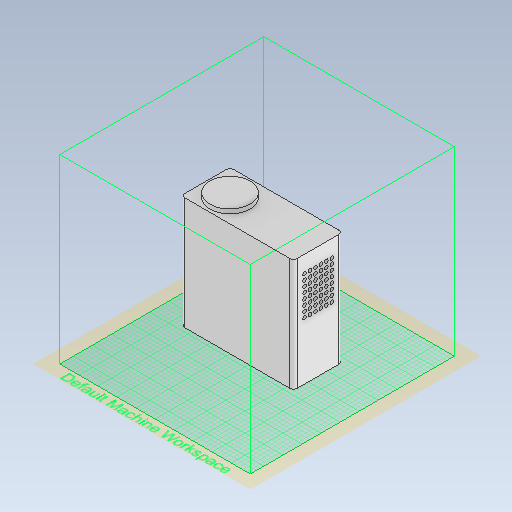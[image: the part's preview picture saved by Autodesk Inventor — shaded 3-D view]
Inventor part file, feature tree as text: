
AUTODESK INVENTOR PART (.ipt)
format: ipt  version: 2021.1 (Build 251245010, 245A)  size: 1,046,016 bytes
history: native  units: in
note: dims shown in document units (in); Inventor stores cm internally (conversion verified against a paired STEP export)
features: extrude x12, other x9, sketch x5, fillet x5, move_body x4, sheet_metal_op x1, boolean_combine x1
ambient origin geometry x8: Origin, YZ Plane, XZ Plane, XY Plane, X Axis, Y Axis, Z Axis, Center Point
bodies: Solid9 (feature_tree), Solid10 (feature_tree), Solid11 (feature_tree)
feature tree (37):
  other  "bottom"
  sheet_metal_op  "face"
  extrude  "Extrusion9"  Depth=4.252in
  extrude  "Extrusion10"  Depth=4.1339in
  extrude  "Extrusion11"  Depth=4.7244in
  extrude  "Extrusion12"  Depth=4.7244in
  extrude  "Extrusion13"  Depth=0.315in
  extrude  "Extrusion14"  Depth=0.1575in
  extrude  "Extrusion15"  Depth=13.7795in
  extrude  "Extrusion16"  Depth=0.5906in
  extrude  "Extrusion17"  Depth=0.5906in
  move_body  "Move Body1"
  move_body  "Move Body2"
  move_body  "Move Body3"
  move_body  "Move Body4"
  extrude  "Extrusion18"  Depth=11.811in TaperAngle=0.0deg
  sketch  "Sketch8"  dims[d6=0.9843in d7=4.7244in]
  extrude  "Extrusion19"  Depth=4.7244in TaperAngle=0.0deg
  extrude  "Extrusion20"  Depth=4.1339in TaperAngle=0.0deg
  fillet  "Fillet1"  Radius=9.7638in
  fillet  "Fillet2"  Radius=0.5487in
  boolean_combine  "Combine1"
  fillet  "Fillet3"  Radius=0.3612in
  fillet  "Fillet4"  Radius=11.811in
  sketch  "Sketch9"  dims[d8=0.315in d9=0.315in d10=0.1575in d11=13.7795in d12=0.5906in d13=0.5906in d30=11.811in d31=0.0in d32=4.7244in d33=0.0in d34=4.1339in d35=0.0in d36=9.7638in d37=0.0in d38=0.5487in d39=0.0in d40=0.3612in d41=0.0in d42=11.811in d43=0.0in d45=0.315in d46=3.1496in d48=0.4724in d49=2.3622in d51=0.4724in d54=1.1265in d55=0.0in d57=3.1496in d59=2.3622in d60=0.315in d61=0.4724in d62=0.4724in d63=0.811in d64=0.0in d65=0.0in d66=0.0in d67=-0.3937in d68=0.0in d69=0.0in d70=-0.3937in d71=0.0in d72=0.0in d73=-0.3937in d74=0.0in d75=0.0in d76=-5.5118in d90=4.7244in d91=4.7244in d92=0.2953in d93=0.2953in d94=0.1575in d95=0.7874in d97=4.1339in d98=0.7874in d100=4.1339in d103=3.5433in d104=0.9843in d105=0.0in d106=0.3937in d107=0.3937in d108=0.7874in d109=0.7874in d110=0.1969in d111=0.1969in d112=0.7874in d113=0.1969in d114=0.0in d115=0.7874in d116=0.0in d117=0.4537in d118=0.3912in d119=0.3912in d120=0.1412in d121=0.2662in]
  fillet  "Fillet5"  Radius=0.315in
  other  "fans"
  other  "TV-BOX"
  other  "Projector"
  other  "top"
  sketch  "Sketch4"  dims[d0=9.7638in d1=4.252in]
  sketch  "Sketch5"  dims[d2=1.1024in d3=4.1339in]
  sketch  "Sketch7"  dims[d4=0.9843in d5=4.7244in]
  other  "Composite1"
  other  "Composite2"
  other  "Srf1"
  other  "Srf2"
